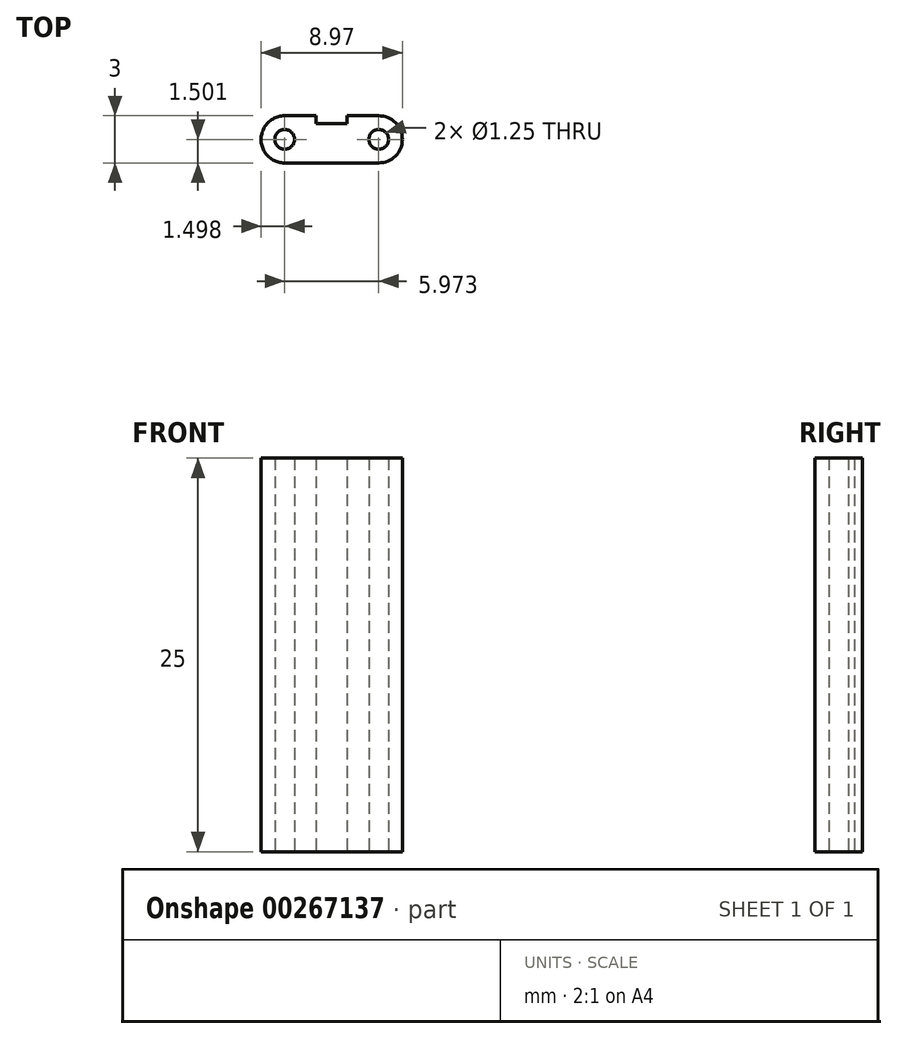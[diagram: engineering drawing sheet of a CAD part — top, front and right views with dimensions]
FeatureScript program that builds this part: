
annotation { "Feature Type Name" : "Feature", "Feature Type Description" : "" }
export const myFeature = defineFeature(function(context is Context, id is Id, definition is map)
    precondition{}
    {
        {
            var Q0;
            Q0=qCreatedBy(makeId("Top.planeOp"),FACE);
            var sketch = newSketch(context, id + "F0", { "sketchPlane" : qUnion([Q0])});
            skCircle(sketch, "E0", {"center": v(-9.96, 8.6) * mm, "radius": 0.62 * mm});
            skCircle(sketch, "E1", {"center": v(-3.99, 8.6) * mm, "radius": 0.62 * mm});
            skLineSegment(sketch, "E2", {"start": v(-9.96, 8.6) * mm, "end": v(-9.96, 10.1) * mm});
            skLineSegment(sketch, "E3", {"start": v(-9.96, 10.1) * mm, "end": v(-9.96, 7.52) * mm});
            skLineSegment(sketch, "E4", {"start": v(-3.99, 8.6) * mm, "end": v(-3.99, 10.1) * mm});
            skLineSegment(sketch, "E5", {"start": v(-3.99, 10.1) * mm, "end": v(-3.99, 7.1) * mm});
            skLineSegment(sketch, "E6", {"start": v(-3.99, 7.1) * mm, "end": v(-9.95, 7.1) * mm});
            skLineSegment(sketch, "E7", {"start": v(-9.96, 7.52) * mm, "end": v(-9.95, 7.1) * mm});
            skPoint(sketch, "E8.orphan", {"position": v(-3.99, 9.95) * mm});
            skArc(sketch, "E9", {"start": v(-9.96, 10.1) * mm, "mid": v(-11.46, 8.59) * mm, "end": v(-9.95, 7.1) * mm});
            skLineSegment(sketch, "E10", {"start": v(-9.96, 8.6) * mm, "end": v(-3.99, 8.6) * mm});
            skArc(sketch, "E11", {"start": v(-3.99, 7.1) * mm, "mid": v(-2.49, 8.6) * mm, "end": v(-3.99, 10.1) * mm});
            skLineSegment(sketch, "E12", {"start": v(-9.96, 10.1) * mm, "end": v(-7.96, 10.1) * mm});
            skLineSegment(sketch, "E13", {"start": v(-7.96, 10.1) * mm, "end": v(-7.96, 9.6) * mm});
            skLineSegment(sketch, "E14", {"start": v(-7.96, 9.6) * mm, "end": v(-5.99, 9.6) * mm});
            skLineSegment(sketch, "E15", {"start": v(-5.99, 9.6) * mm, "end": v(-5.99, 10.1) * mm});
            skLineSegment(sketch, "E16", {"start": v(-5.99, 10.1) * mm, "end": v(-3.99, 10.1) * mm});
            skSolve(sketch);
        }
        {
            var Q0;
            Q0 = qSketchRegion(id + "F0", true);
            extrude(context, id + "F1", {"entities" : qUnion([Q0]), "depth" : 25 * mm});
        }
    });
